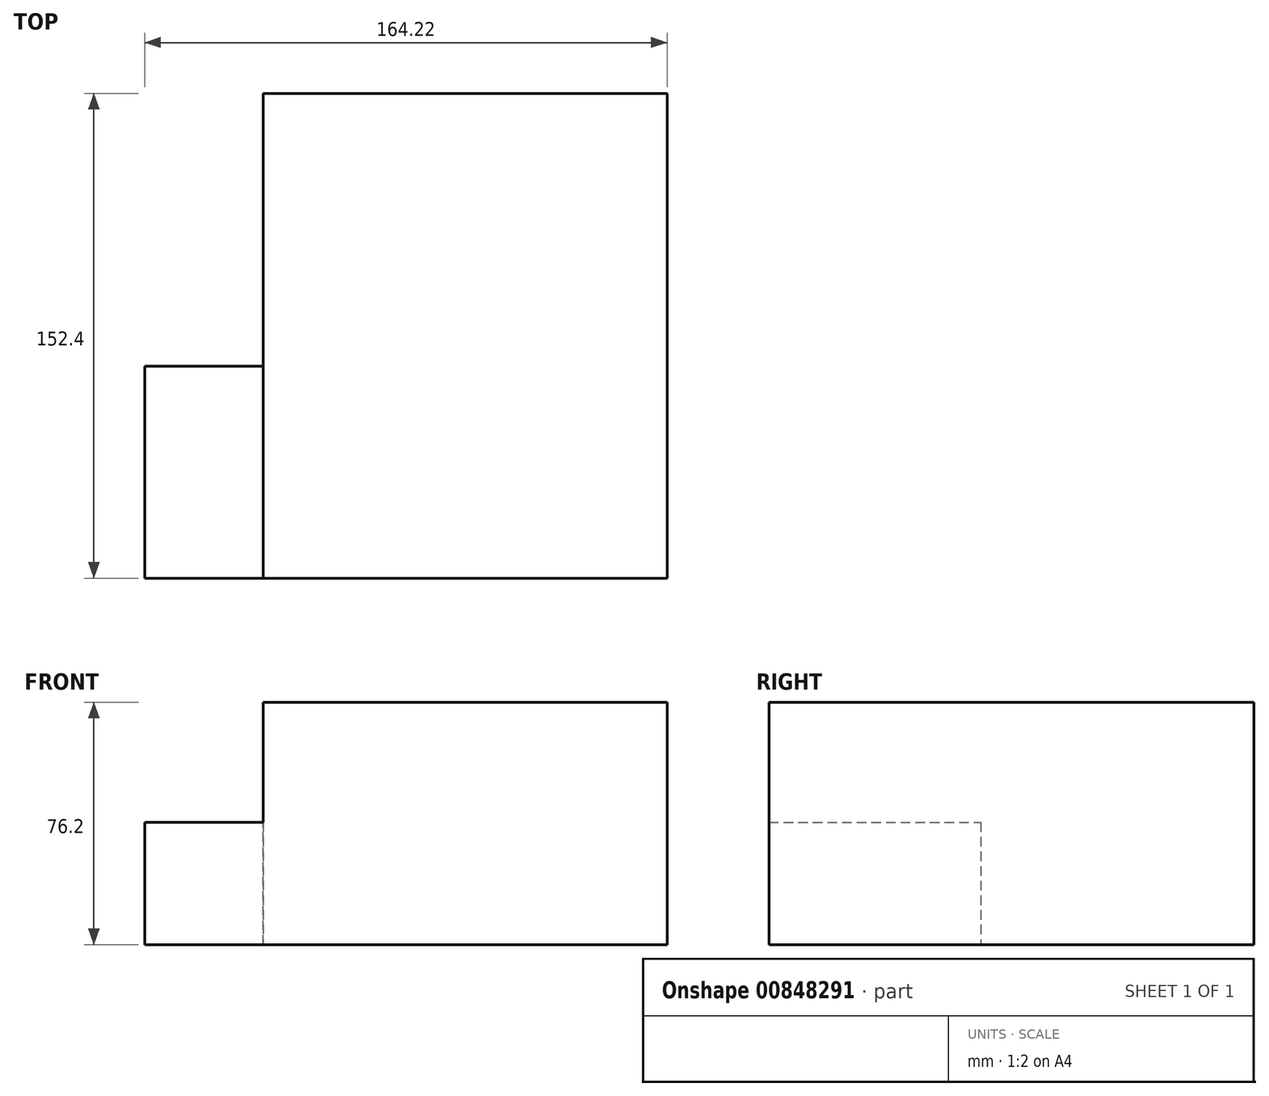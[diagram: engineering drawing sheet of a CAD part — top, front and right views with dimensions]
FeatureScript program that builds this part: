
annotation { "Feature Type Name" : "Feature", "Feature Type Description" : "" }
export const myFeature = defineFeature(function(context is Context, id is Id, definition is map)
    precondition{}
    {
        {
            var Q0;
            Q0=qCreatedBy(makeId("Top.planeOp"),FACE);
            var sketch = newSketch(context, id + "F0", { "sketchPlane" : qUnion([Q0])});
            skLineSegment(sketch, "E0", {"start": v(-77.08, 0) * mm, "end": v(49.92, 0) * mm});
            skLineSegment(sketch, "E1", {"start": v(49.92, 0) * mm, "end": v(49.92, 152.4) * mm});
            skLineSegment(sketch, "E2", {"start": v(49.92, 152.4) * mm, "end": v(-77.08, 152.4) * mm});
            skLineSegment(sketch, "E3", {"start": v(-77.08, 152.4) * mm, "end": v(-77.08, 0) * mm});
            skSolve(sketch);
        }
        {
            var Q0;
            Q0=qCreatedBy(makeId("Right.planeOp"),FACE);
            var sketch = newSketch(context, id + "F1", { "sketchPlane" : qUnion([Q0])});
            skLineSegment(sketch, "E4", {"start": v(0, 0) * mm, "end": v(0, 76.2) * mm});
            skSolve(sketch);
        }
        {
            var Q0;
            Q0=makeQuery(id+"F0.imprint","IMPRINT",FACE,{"disambiguationData":[TD([[makeQuery(id+"F0.imprint","IMPRINT",EDGE,{"derivedFrom":sQuery(id+"F0.wireOp",EDGE,"E0")}),1.0]])]});
            var Q1;
            Q1=sQuery(id+"F1.wireOp",EDGE,"E4");
            sweep(context, id + "F2", {"profiles" : qUnion([Q0]), "path" : qUnion([Q1])});
        }
        {
            var Q0;
            Q0=qCreatedBy(makeId("Top.planeOp"),FACE);
            var sketch = newSketch(context, id + "F3", { "sketchPlane" : qUnion([Q0])});
            skLineSegment(sketch, "E5", {"start": v(0, 0) * mm, "end": v(-114.3, 0) * mm});
            skLineSegment(sketch, "E6", {"start": v(-114.3, 66.61) * mm, "end": v(0, 66.61) * mm});
            skLineSegment(sketch, "E7", {"start": v(0, 66.61) * mm, "end": v(0, 0) * mm});
            skLineSegment(sketch, "E8", {"start": v(-114.3, 0) * mm, "end": v(-114.3, 66.61) * mm});
            skLineSegment(sketch, "E9", {"start": v(-114.3, 20.37) * mm, "end": v(0, 20.37) * mm});
            skLineSegment(sketch, "E10", {"start": v(-114.3, 44.04) * mm, "end": v(0, 44.04) * mm});
            skLineSegment(sketch, "E11", {"start": v(-57.15, 66.61) * mm, "end": v(-57.15, 0) * mm});
            skSolve(sketch);
        }
        {
            var Q0;
            Q0=qCreatedBy(makeId("Right.planeOp"),FACE);
            var sketch = newSketch(context, id + "F4", { "sketchPlane" : qUnion([Q0])});
            skLineSegment(sketch, "E12", {"start": v(0, 0) * mm, "end": v(0, 38.44) * mm});
            skSolve(sketch);
        }
        {
            var Q0;
            {var subQ0=sQuery(id+"F3.wireOp",EDGE,"E7");var subQ1=sQuery(id+"F3.wireOp",EDGE,"E5");var subQ2=makeQuery(id+"F3.imprint","INTERSECT",VERTEX,{"derivedFrom":[subQ1,subQ0]});Q0=makeQuery(id+"F3.imprint","IMPRINT",FACE,{"disambiguationData":[TD([[makeQuery(id+"F3.imprint","IMPRINT",EDGE,{"disambiguationData":[TD([[subQ2,-1.0]])],"derivedFrom":subQ1}),-1.0]])]});}
            var Q1;
            {var subQ0=sQuery(id+"F3.wireOp",EDGE,"E8");var subQ1=sQuery(id+"F3.wireOp",EDGE,"E5");var subQ2=makeQuery(id+"F3.imprint","INTERSECT",VERTEX,{"derivedFrom":[subQ1,subQ0]});Q1=makeQuery(id+"F3.imprint","IMPRINT",FACE,{"disambiguationData":[TD([[makeQuery(id+"F3.imprint","IMPRINT",EDGE,{"disambiguationData":[TD([[subQ2,1.0]])],"derivedFrom":subQ1}),-1.0]])]});}
            var Q2;
            {var subQ0=sQuery(id+"F3.wireOp",EDGE,"E9");var subQ1=sQuery(id+"F3.wireOp",EDGE,"E8");var subQ2=makeQuery(id+"F3.imprint","INTERSECT",VERTEX,{"derivedFrom":[subQ1,subQ0]});Q2=makeQuery(id+"F3.imprint","IMPRINT",FACE,{"disambiguationData":[TD([[makeQuery(id+"F3.imprint","IMPRINT",EDGE,{"disambiguationData":[TD([[subQ2,-1.0]])],"derivedFrom":subQ1}),-1.0]])]});}
            var Q3;
            {var subQ0=sQuery(id+"F3.wireOp",EDGE,"E9");var subQ1=sQuery(id+"F3.wireOp",EDGE,"E7");var subQ2=makeQuery(id+"F3.imprint","INTERSECT",VERTEX,{"derivedFrom":[subQ1,subQ0]});Q3=makeQuery(id+"F3.imprint","IMPRINT",FACE,{"disambiguationData":[TD([[makeQuery(id+"F3.imprint","IMPRINT",EDGE,{"disambiguationData":[TD([[subQ2,1.0]])],"derivedFrom":subQ1}),-1.0]])]});}
            var Q4;
            {var subQ0=sQuery(id+"F3.wireOp",EDGE,"E7");var subQ1=sQuery(id+"F3.wireOp",EDGE,"E6");var subQ2=makeQuery(id+"F3.imprint","INTERSECT",VERTEX,{"derivedFrom":[subQ1,subQ0]});Q4=makeQuery(id+"F3.imprint","IMPRINT",FACE,{"disambiguationData":[TD([[makeQuery(id+"F3.imprint","IMPRINT",EDGE,{"disambiguationData":[TD([[subQ2,1.0]])],"derivedFrom":subQ1}),-1.0]])]});}
            var Q5;
            {var subQ0=sQuery(id+"F3.wireOp",EDGE,"E8");var subQ1=sQuery(id+"F3.wireOp",EDGE,"E6");var subQ2=makeQuery(id+"F3.imprint","INTERSECT",VERTEX,{"derivedFrom":[subQ1,subQ0]});Q5=makeQuery(id+"F3.imprint","IMPRINT",FACE,{"disambiguationData":[TD([[makeQuery(id+"F3.imprint","IMPRINT",EDGE,{"disambiguationData":[TD([[subQ2,-1.0]])],"derivedFrom":subQ1}),-1.0]])]});}
            var Q6;
            Q6=sQuery(id+"F4.wireOp",EDGE,"E12");
            sweep(context, id + "F5", {"profiles" : qUnion([Q0, Q1, Q2, Q3, Q4, Q5]), "path" : qUnion([Q6])});
        }
        {
            var Q0;
            Q0=qCreatedBy(makeId("Top.planeOp"),FACE);
            var sketch = newSketch(context, id + "F6", { "sketchPlane" : qUnion([Q0])});
            skLineSegment(sketch, "E13", {"start": v(0, 0) * mm, "end": v(-67.56, 0) * mm});
            skLineSegment(sketch, "E14", {"start": v(-67.56, 0) * mm, "end": v(-67.56, 47.5) * mm});
            skLineSegment(sketch, "E15", {"start": v(-67.56, 47.5) * mm, "end": v(0, 47.5) * mm});
            skLineSegment(sketch, "E16", {"start": v(0, 47.5) * mm, "end": v(0, 0) * mm});
            skSolve(sketch);
        }
        {
            var Q0;
            Q0=qCreatedBy(makeId("Right.planeOp"),FACE);
            var sketch = newSketch(context, id + "F7", { "sketchPlane" : qUnion([Q0])});
            skLineSegment(sketch, "E17", {"start": v(0, 0) * mm, "end": v(0, 12.7) * mm});
            skSolve(sketch);
        }
        {
            var Q0;
            Q0=makeQuery(id+"F6.imprint","IMPRINT",FACE,{"disambiguationData":[TD([[makeQuery(id+"F6.imprint","IMPRINT",EDGE,{"derivedFrom":sQuery(id+"F6.wireOp",EDGE,"E13")}),-1.0]])]});
            var Q1;
            Q1=sQuery(id+"F7.wireOp",EDGE,"E17");
            sweep(context, id + "F8", {"profiles" : qUnion([Q0]), "path" : qUnion([Q1])});
        }
        {
            var Q0;
            Q0=qCreatedBy(makeId("Right.planeOp"),FACE);
            var sketch = newSketch(context, id + "F9", { "sketchPlane" : qUnion([Q0])});
            skLineSegment(sketch, "E18", {"start": v(0, 0) * mm, "end": v(0, 12.7) * mm});
            skLineSegment(sketch, "E19", {"start": v(0, 12.7) * mm, "end": v(0, 76.2) * mm});
            skLineSegment(sketch, "E20", {"start": v(0, 76.2) * mm, "end": v(8.38, 76.2) * mm});
            skLineSegment(sketch, "E21", {"start": v(8.38, 76.2) * mm, "end": v(8.38, 12.7) * mm});
            skLineSegment(sketch, "E22", {"start": v(8.38, 12.7) * mm, "end": v(0, 12.7) * mm});
            skSolve(sketch);
        }
        {
            var Q0;
            Q0=qCreatedBy(makeId("Front.planeOp"),FACE);
            var sketch = newSketch(context, id + "F10", { "sketchPlane" : qUnion([Q0])});
            skLineSegment(sketch, "E23", {"start": v(0, 0) * mm, "end": v(0, 12.7) * mm});
            skLineSegment(sketch, "E24", {"start": v(0, 12.7) * mm, "end": v(-8.38, 12.7) * mm});
            skSolve(sketch);
        }
        {
            var Q0;
            Q0=makeQuery(id+"F9.imprint","IMPRINT",FACE,{"disambiguationData":[TD([[makeQuery(id+"F9.imprint","IMPRINT",EDGE,{"derivedFrom":sQuery(id+"F9.wireOp",EDGE,"E19")}),-1.0]])]});
            var Q1;
            Q1=sQuery(id+"F10.wireOp",EDGE,"E24");
            sweep(context, id + "F11", {"operationType" : NewBodyOperationType.ADD, "profiles" : qUnion([Q0]), "path" : qUnion([Q1])});
        }
    });
